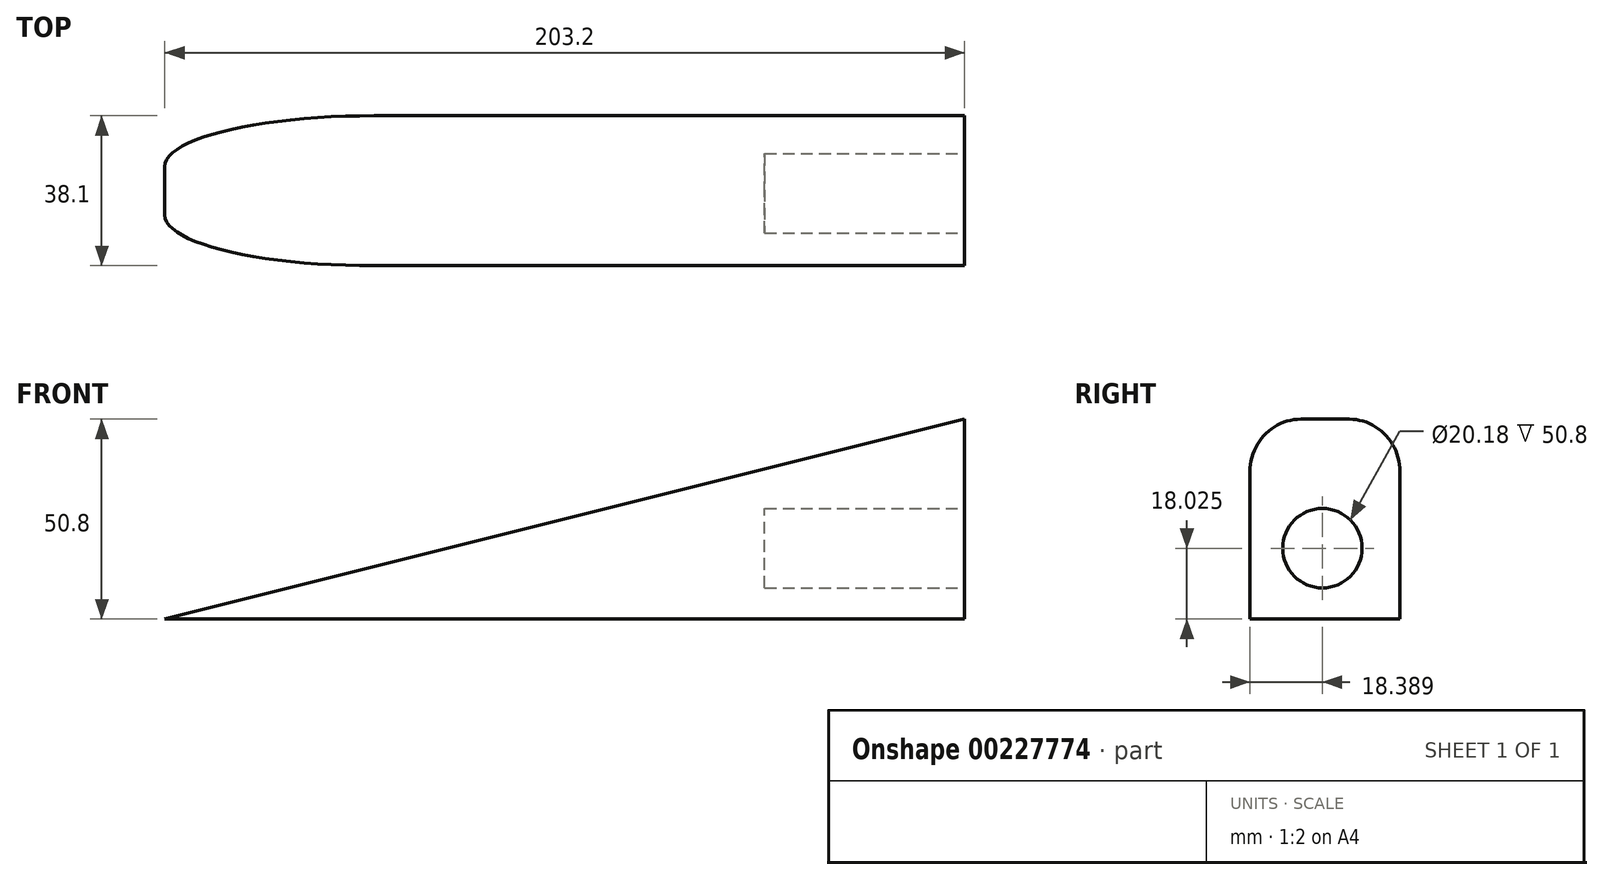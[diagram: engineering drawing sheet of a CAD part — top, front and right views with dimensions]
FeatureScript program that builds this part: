
annotation { "Feature Type Name" : "Feature", "Feature Type Description" : "" }
export const myFeature = defineFeature(function(context is Context, id is Id, definition is map)
    precondition{}
    {
        {
            var Q0;
            Q0=qCreatedBy(makeId("Front.planeOp"),FACE);
            var sketch = newSketch(context, id + "F0", { "sketchPlane" : qUnion([Q0])});
            skLineSegment(sketch, "E0", {"start": v(99.27, 0) * mm, "end": v(-103.93, 0) * mm});
            skLineSegment(sketch, "E1", {"start": v(99.27, 0) * mm, "end": v(99.27, 50.8) * mm});
            skLineSegment(sketch, "E2", {"start": v(99.27, 50.8) * mm, "end": v(-103.93, 0) * mm});
            skSolve(sketch);
        }
        {
            var Q0;
            Q0=makeQuery(id+"F0.imprint","IMPRINT",FACE,{"disambiguationData":[TD([[makeQuery(id+"F0.imprint","IMPRINT",EDGE,{"derivedFrom":sQuery(id+"F0.wireOp",EDGE,"E0")}),-1.0]])]});
            extrude(context, id + "F1", {"entities" : qUnion([Q0]), "depth" : 38.1 * mm});
        }
        {
            var Q0;
            Q0=makeQuery(id+"F1.opExtrude","CAP_EDGE",EDGE,{"disambiguationData":[OSD([sQuery(id+"F0.wireOp",EDGE,"E2")])],"isStart":true});
            var Q1;
            Q1=makeQuery(id+"F1.opExtrude","CAP_EDGE",EDGE,{"disambiguationData":[OSD([sQuery(id+"F0.wireOp",EDGE,"E2")])],"isStart":false});
            fillet(context, id + "F2", {"entities" : qUnion([Q0, Q1]), "radius" : 12.88 * mm, "tangentPropagation" : true, "allowEdgeOverflow" : false});
        }
        {
            var Q0;
            Q0=makeQuery(id+"F1.opExtrude","SWEPT_FACE",FACE,{"disambiguationData":[OSD([sQuery(id+"F0.wireOp",EDGE,"E1")])]});
            var sketch = newSketch(context, id + "F3", { "sketchPlane" : qUnion([Q0])});
            skCircle(sketch, "E3", {"center": v(-19.71, 18.02) * mm, "radius": 10.09 * mm});
            skSolve(sketch);
        }
        {
            var Q0;
            Q0=makeQuery(id+"F3.imprint","IMPRINT",FACE,{"disambiguationData":[TD([[makeQuery(id+"F3.imprint","IMPRINT",EDGE,{"derivedFrom":sQuery(id+"F3.wireOp",EDGE,"E3")}),1.0]])]});
            extrude(context, id + "F4", {"entities" : qUnion([Q0]), "operationType" : NewBodyOperationType.REMOVE, "oppositeDirection" : true, "depth" : 50.8 * mm});
        }
    });
